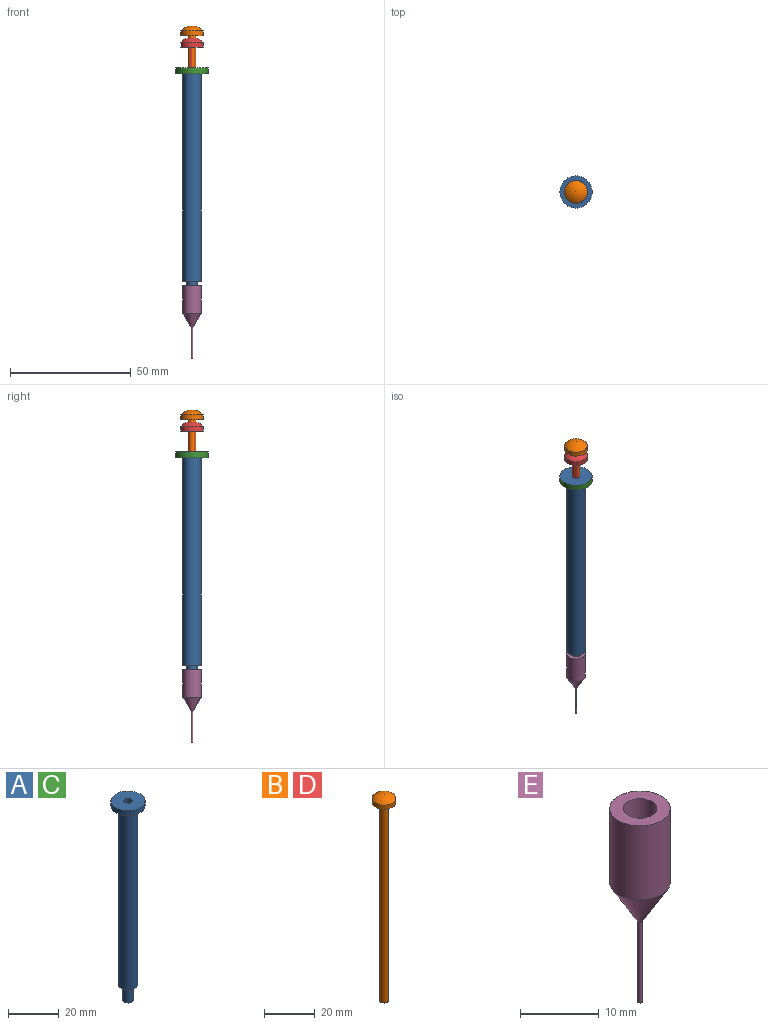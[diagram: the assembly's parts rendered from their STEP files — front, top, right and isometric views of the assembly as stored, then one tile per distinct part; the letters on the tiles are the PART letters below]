
ASSEMBLY  parts=5 mates=2
PART A: 10 faces, bbox 13.4x13.4x96 mm
  f0: cylinder r=0.25mm len=9.12mm, axis (0,0,1), area 14.3mm2, adj f1,f9
  f1: plane 3.25x3.25mm, normal (0,0,1), area 8.1mm2, adj f0,f2
  f2: cylinder r=1.62mm len=86.88mm, axis (0,0,1), area 887.1mm2, adj f1,f3
  f3: plane 13.4x13.4mm, normal (0,0,1), area 132.7mm2, adj f2,f4
  f4: cylinder r=6.7mm len=13.4mm, axis (0,0,1), area 101mm2, adj f3,f5
  f5: plane 13.4x13.4mm, normal (0,0,-1), area 94.7mm2, adj f4,f6
  f6: cylinder r=3.84mm len=85.98mm, axis (0,0,1), area 2074.5mm2, adj f5,f7
  f7: plane 7.68x7.68mm, normal (0,0,-1), area 31.8mm2, adj f6,f8
  f8: cylinder r=2.15mm len=7.62mm, axis (0,0,1), area 102.9mm2, adj f7,f9
  f9: plane 4.3x4.3mm, normal (0,0,-1), area 14.3mm2, adj f0,f8
PART B: 5 faces, bbox 9.4x9.4x99.5 mm
  f0: cylinder r=1.62mm len=95.5mm, axis (0,0,1), area 975.1mm2, adj f1,f4
  f1: plane 3.25x3.25mm, normal (0,0,-1), area 8.3mm2, adj f0
  f2: sphere r=6.52mm, area 82mm2, adj f3
  f3: cylinder r=4.7mm len=9.4mm, axis (0,0,1), area 59.1mm2, adj f2,f4
  f4: plane 9.4x9.4mm, normal (0,0,-1), area 61.1mm2, adj f0,f3
PART C: same geometry as A
PART D: same geometry as B
PART E: 7 faces, bbox 7.7x7.7x30 mm
  f0: cylinder r=2.15mm len=5.62mm, axis (0,0,1), area 75.9mm2, adj f1,f6
  f1: plane 7.68x7.68mm, normal (0,0,1), area 31.8mm2, adj f0,f2
  f2: cylinder r=3.84mm len=11.5mm, axis (0,0,1), area 277.5mm2, adj f1,f3
  f3: cone r=3.84mm half-angle=30.5deg, axis (0,0,1), area 90.6mm2, adj f2,f4
  f4: cylinder r=0.3mm len=12.5mm, axis (0,0,1), area 23.6mm2, adj f3,f5
  f5: plane 0.6x0.6mm, normal (0,0,-1), area 0.3mm2, adj f4
  f6: plane 4.3x4.3mm, normal (0,0,1), area 14.5mm2, adj f0
PLACE A at identity
PLACE B rot(axis=(0,0,-1),95.3deg) t=(0,0,4.78)mm
PLACE C at identity fixed
PLACE D at identity
PLACE E t=(0,0,0.13)mm
MATE fastened E.f0 <-> C.f0  axis (0,0,1) through (0,0,-96)mm
MATE cylindrical B.f0 <-> C.f0  axis (0,0,1) through (0,0,-82.1)mm
